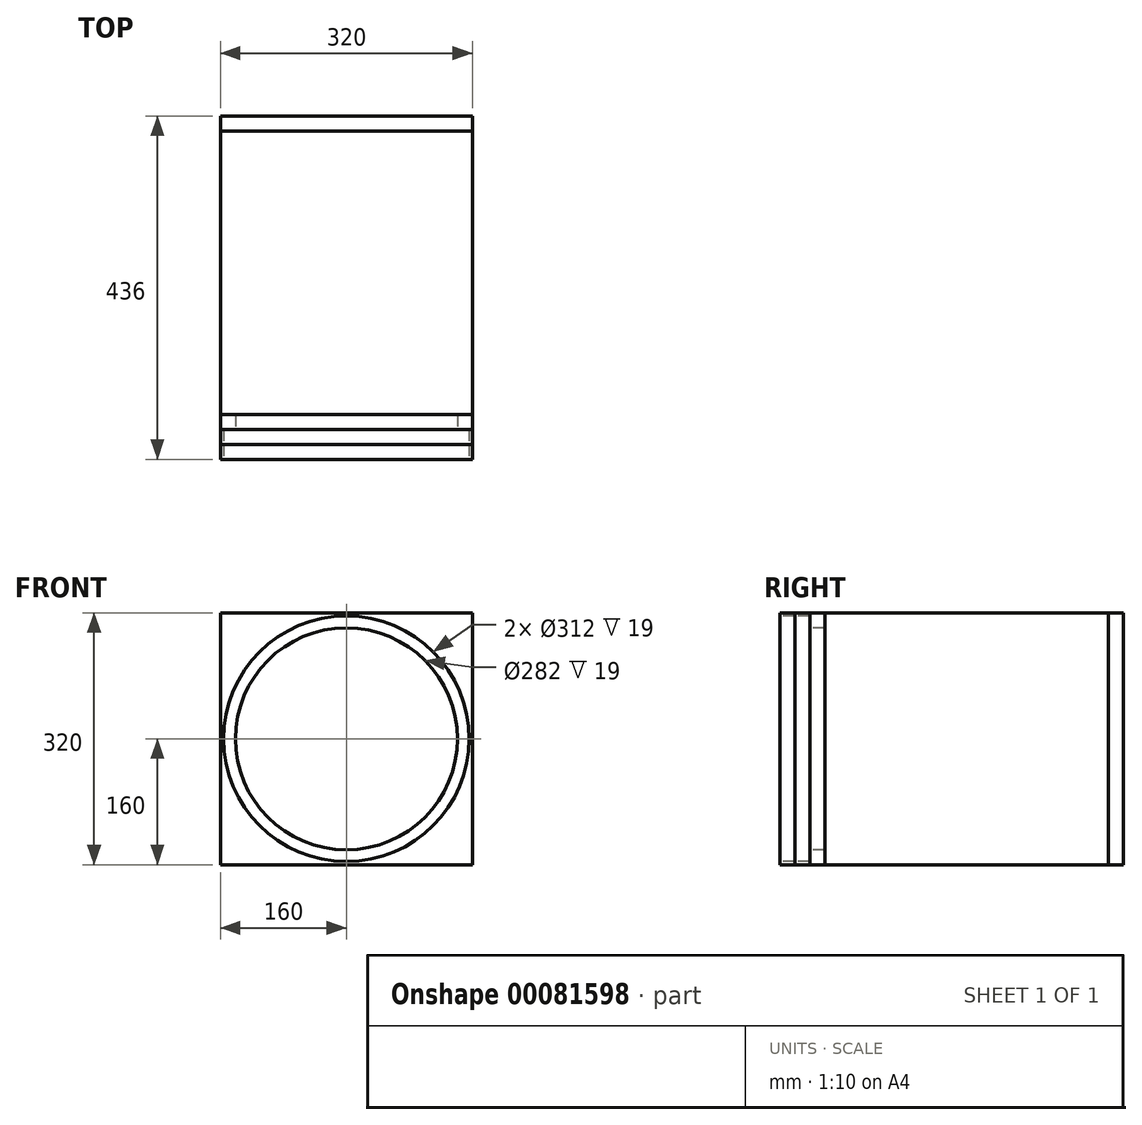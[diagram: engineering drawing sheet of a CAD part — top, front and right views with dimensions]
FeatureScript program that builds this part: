
annotation { "Feature Type Name" : "Feature", "Feature Type Description" : "" }
export const myFeature = defineFeature(function(context is Context, id is Id, definition is map)
    precondition{}
    {
        {
            var Q0;
            Q0=qCreatedBy(makeId("Front.planeOp"),FACE);
            var sketch = newSketch(context, id + "F0", { "sketchPlane" : qUnion([Q0])});
            skLineSegment(sketch, "E0.bottom", {"start": v(0, 0) * mm, "end": v(320, 0) * mm});
            skLineSegment(sketch, "E0.top", {"start": v(0, 320) * mm, "end": v(320, 320) * mm});
            skLineSegment(sketch, "E0.left", {"start": v(0, 0) * mm, "end": v(0, 320) * mm});
            skLineSegment(sketch, "E0.right", {"start": v(320, 0) * mm, "end": v(320, 320) * mm});
            skSolve(sketch);
        }
        {
            var Q0;
            Q0=makeQuery(id+"F0.imprint","IMPRINT",FACE,{"disambiguationData":[TD([[makeQuery(id+"F0.imprint","IMPRINT",EDGE,{"derivedFrom":sQuery(id+"F0.wireOp",EDGE,"E0.bottom")}),1.0]])]});
            extrude(context, id + "F1", {"entities" : qUnion([Q0]), "oppositeDirection" : true, "depth" : 360 * mm});
        }
        {
            var Q0;
            Q0=qCreatedBy(makeId("Front.planeOp"),FACE);
            var sketch = newSketch(context, id + "F2", { "sketchPlane" : qUnion([Q0])});
            skLineSegment(sketch, "E1.bottom", {"start": v(0, 0) * mm, "end": v(320, 0) * mm});
            skLineSegment(sketch, "E1.top", {"start": v(0, 320) * mm, "end": v(320, 320) * mm});
            skLineSegment(sketch, "E1.left", {"start": v(0, 0) * mm, "end": v(0, 320) * mm});
            skLineSegment(sketch, "E1.right", {"start": v(320, 0) * mm, "end": v(320, 320) * mm});
            skSolve(sketch);
        }
        {
            var Q0;
            Q0 = qSketchRegion(id + "F2", true);
            extrude(context, id + "F3", {"entities" : qUnion([Q0]), "depth" : 19 * mm});
        }
        {
            var Q0;
            Q0=makeQuery(id+"F3.opExtrude","SWEPT_BODY",BODY,{"disambiguationData":[OSD([sQuery(id+"F2.wireOp",EDGE,"E1.bottom"),sQuery(id+"F2.wireOp",EDGE,"E1.top"),sQuery(id+"F2.wireOp",EDGE,"E1.left"),sQuery(id+"F2.wireOp",EDGE,"E1.right")])]});
            transform(context, id + "F4", {"entities" : qUnion([Q0]), "transformType" : TransformType.TRANSLATION_3D, "dx" : 0 * mm, "dy" : -19 * mm, "dz" : 0 * mm, "makeCopy" : true});
        }
        {
            var Q0;
            Q0=makeQuery(id+"F3.opExtrude","SWEPT_BODY",BODY,{"disambiguationData":[OSD([sQuery(id+"F2.wireOp",EDGE,"E1.bottom"),sQuery(id+"F2.wireOp",EDGE,"E1.top"),sQuery(id+"F2.wireOp",EDGE,"E1.left"),sQuery(id+"F2.wireOp",EDGE,"E1.right")])]});
            transform(context, id + "F5", {"entities" : qUnion([Q0]), "transformType" : TransformType.TRANSLATION_3D, "dx" : 0 * mm, "dy" : 379 * mm, "dz" : 0 * mm, "makeCopy" : true});
        }
        {
            var Q0;
            Q0=makeQuery(id+"F4.opPattern","COPY",FACE,{"derivedFrom":makeQuery(id+"F3.opExtrude","CAP_FACE",FACE,{"disambiguationData":[OSD([sQuery(id+"F2.wireOp",EDGE,"E1.bottom"),sQuery(id+"F2.wireOp",EDGE,"E1.top"),sQuery(id+"F2.wireOp",EDGE,"E1.left"),sQuery(id+"F2.wireOp",EDGE,"E1.right")])],"isStart":false}),"instanceName":"1"});
            var sketch = newSketch(context, id + "F6", { "sketchPlane" : qUnion([Q0])});
            skCircle(sketch, "E2", {"center": v(160, 160) * mm, "radius": 156 * mm});
            skPoint(sketch, "E2.centerSnap0", {"position": v(160, 0) * mm});
            skPoint(sketch, "E2.centerSnap1", {"position": v(0, 160) * mm});
            skSolve(sketch);
        }
        {
            var Q0;
            Q0=makeQuery(id+"F6.imprint","IMPRINT",FACE,{"disambiguationData":[TD([[makeQuery(id+"F6.imprint","IMPRINT",EDGE,{"derivedFrom":sQuery(id+"F6.wireOp",EDGE,"E2")}),1.0]])]});
            var Q1;
            Q1=makeQuery(id+"F4.opPattern","COPY",BODY,{"derivedFrom":makeQuery(id+"F3.opExtrude","SWEPT_BODY",BODY,{"disambiguationData":[OSD([sQuery(id+"F2.wireOp",EDGE,"E1.bottom"),sQuery(id+"F2.wireOp",EDGE,"E1.top"),sQuery(id+"F2.wireOp",EDGE,"E1.left"),sQuery(id+"F2.wireOp",EDGE,"E1.right")])]}),"instanceName":"1"});
            extrude(context, id + "F7", {"entities" : qUnion([Q0]), "operationType" : NewBodyOperationType.REMOVE, "endBound" : BoundingType.UP_TO_BODY, "oppositeDirection" : true, "endBoundEntityBody" : qUnion([Q1]), "depth" : 25 * mm});
        }
        {
            var Q0;
            Q0=makeQuery(id+"F3.opExtrude","CAP_FACE",FACE,{"disambiguationData":[OSD([sQuery(id+"F2.wireOp",EDGE,"E1.bottom"),sQuery(id+"F2.wireOp",EDGE,"E1.top"),sQuery(id+"F2.wireOp",EDGE,"E1.left"),sQuery(id+"F2.wireOp",EDGE,"E1.right")])],"isStart":false});
            var sketch = newSketch(context, id + "F8", { "sketchPlane" : qUnion([Q0])});
            skCircle(sketch, "E3", {"center": v(160, 160) * mm, "radius": 141 * mm});
            skPoint(sketch, "E3.centerSnap0", {"position": v(160, 0) * mm});
            skPoint(sketch, "E3.centerSnap1", {"position": v(0, 160) * mm});
            skSolve(sketch);
        }
        {
            var Q0;
            Q0=makeQuery(id+"F8.imprint","IMPRINT",FACE,{"disambiguationData":[TD([[makeQuery(id+"F8.imprint","IMPRINT",EDGE,{"derivedFrom":sQuery(id+"F8.wireOp",EDGE,"E3")}),1.0]])]});
            var Q1;
            Q1=makeQuery(id+"F3.opExtrude","SWEPT_BODY",BODY,{"disambiguationData":[OSD([sQuery(id+"F2.wireOp",EDGE,"E1.bottom"),sQuery(id+"F2.wireOp",EDGE,"E1.top"),sQuery(id+"F2.wireOp",EDGE,"E1.left"),sQuery(id+"F2.wireOp",EDGE,"E1.right")])]});
            extrude(context, id + "F9", {"entities" : qUnion([Q0]), "operationType" : NewBodyOperationType.REMOVE, "endBound" : BoundingType.UP_TO_BODY, "oppositeDirection" : true, "endBoundEntityBody" : qUnion([Q1]), "depth" : 25 * mm});
        }
        {
            var Q0;
            Q0=makeQuery(id+"F4.opPattern","COPY",BODY,{"derivedFrom":makeQuery(id+"F3.opExtrude","SWEPT_BODY",BODY,{"disambiguationData":[OSD([sQuery(id+"F2.wireOp",EDGE,"E1.bottom"),sQuery(id+"F2.wireOp",EDGE,"E1.top"),sQuery(id+"F2.wireOp",EDGE,"E1.left"),sQuery(id+"F2.wireOp",EDGE,"E1.right")])]}),"instanceName":"1"});
            transform(context, id + "F10", {"entities" : qUnion([Q0]), "transformType" : TransformType.TRANSLATION_3D, "dx" : 0 * mm, "dy" : -19 * mm, "dz" : 0 * mm, "makeCopy" : true});
        }
    });
